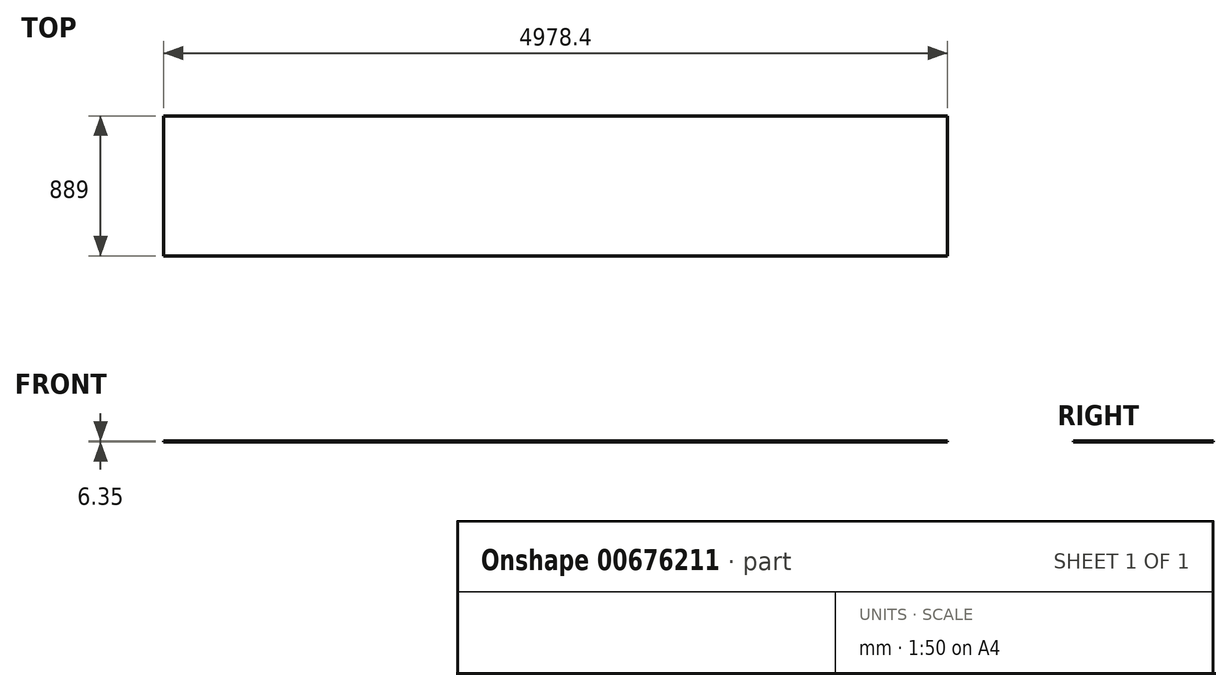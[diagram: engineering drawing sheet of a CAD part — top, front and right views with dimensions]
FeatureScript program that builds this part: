
annotation { "Feature Type Name" : "Feature", "Feature Type Description" : "" }
export const myFeature = defineFeature(function(context is Context, id is Id, definition is map)
    precondition{}
    {
        {
            var Q0;
            Q0=qCreatedBy(makeId("Top.planeOp"),FACE);
            var sketch = newSketch(context, id + "F0", { "sketchPlane" : qUnion([Q0])});
            skLineSegment(sketch, "E0.bottom", {"start": v(-2489.2, -444.5) * mm, "end": v(2489.2, -444.5) * mm});
            skLineSegment(sketch, "E0.top", {"start": v(-2489.2, 444.5) * mm, "end": v(2489.2, 444.5) * mm});
            skLineSegment(sketch, "E0.left", {"start": v(-2489.2, -444.5) * mm, "end": v(-2489.2, 444.5) * mm});
            skLineSegment(sketch, "E0.right", {"start": v(2489.2, -444.5) * mm, "end": v(2489.2, 444.5) * mm});
            skPoint(sketch, "E0.middle", {"position": v(0, 0) * mm});
            skSolve(sketch);
        }
        {
            var Q0;
            Q0=makeQuery(id+"F0.imprint","IMPRINT",FACE,{"disambiguationData":[TD([[makeQuery(id+"F0.imprint","IMPRINT",EDGE,{"derivedFrom":sQuery(id+"F0.wireOp",EDGE,"E0.bottom")}),1.0]])]});
            extrude(context, id + "F1", {"entities" : qUnion([Q0]), "depth" : 6.35 * mm, "offsetDistance" : 25.4 * mm});
        }
    });
